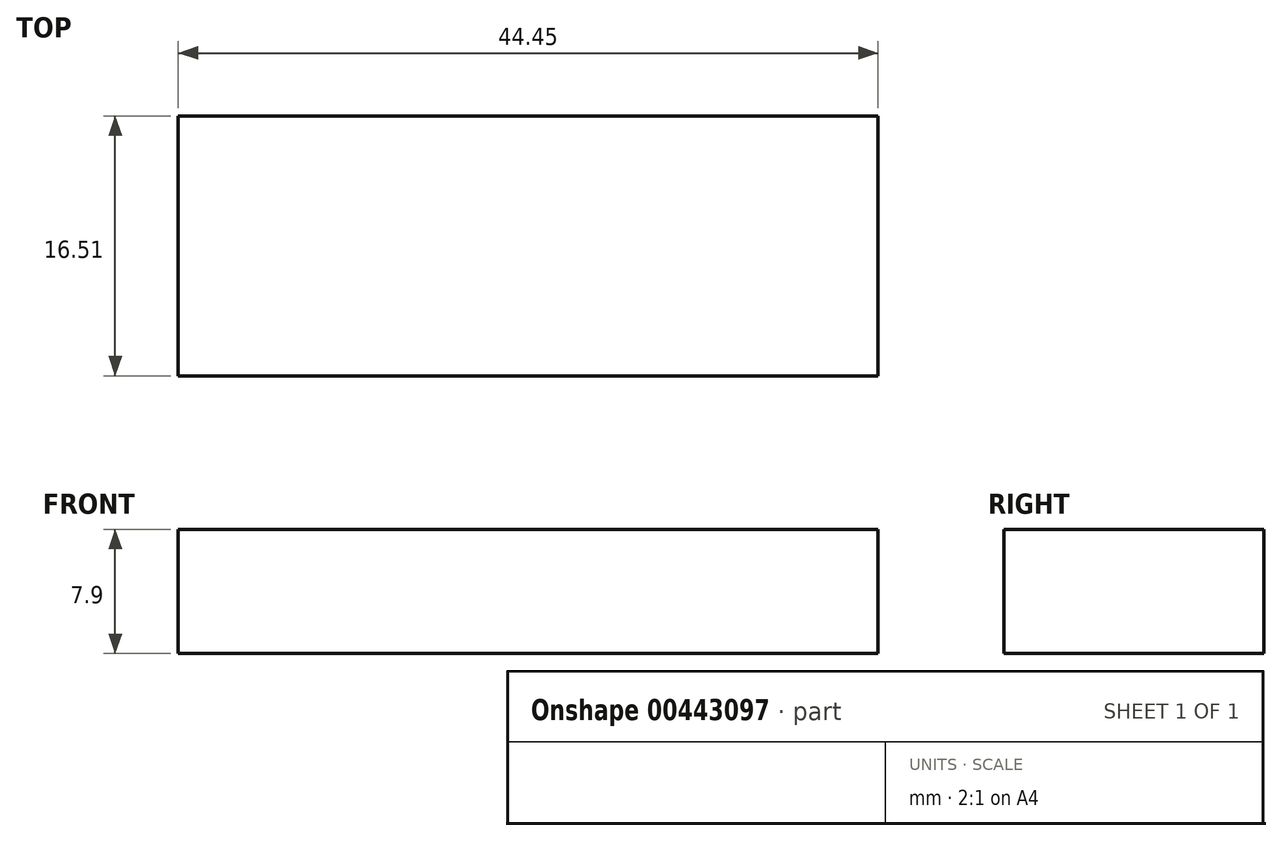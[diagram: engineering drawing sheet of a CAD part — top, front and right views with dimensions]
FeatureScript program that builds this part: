
annotation { "Feature Type Name" : "Feature", "Feature Type Description" : "" }
export const myFeature = defineFeature(function(context is Context, id is Id, definition is map)
    precondition{}
    {
        {
            var Q0;
            Q0=qCreatedBy(makeId("Top.planeOp"),FACE);
            var sketch = newSketch(context, id + "F0", { "sketchPlane" : qUnion([Q0])});
            skLineSegment(sketch, "E0.bottom", {"start": v(0, 0) * mm, "end": v(-50.8, 0) * mm});
            skLineSegment(sketch, "E0.top", {"start": v(0, 25.4) * mm, "end": v(-50.8, 25.4) * mm});
            skLineSegment(sketch, "E0.left", {"start": v(0, 0) * mm, "end": v(0, 25.4) * mm});
            skLineSegment(sketch, "E0.right", {"start": v(-50.8, 0) * mm, "end": v(-50.8, 25.4) * mm});
            skLineSegment(sketch, "E1.bottom", {"start": v(-44.45, 16.51) * mm, "end": v(0, 16.51) * mm});
            skLineSegment(sketch, "E1.top", {"start": v(-44.45, 0) * mm, "end": v(0, 0) * mm});
            skLineSegment(sketch, "E1.left", {"start": v(-44.45, 16.51) * mm, "end": v(-44.45, 0) * mm});
            skLineSegment(sketch, "E1.right", {"start": v(0, 16.51) * mm, "end": v(0, 0) * mm});
            skSolve(sketch);
        }
        {
            var Q0;
            Q0=makeQuery(id+"F0.imprint","IMPRINT",FACE,{"disambiguationData":[TD([[makeQuery(id+"F0.imprint","IMPRINT",EDGE,{"derivedFrom":sQuery(id+"F0.wireOp",EDGE,"E0.bottom")}),-1.0]])]});
            extrude(context, id + "F1", {"entities" : qUnion([Q0]), "depth" : 7.9 * mm});
        }
        {
            var Q0;
            Q0=makeQuery(id+"F1.opExtrude","CAP_FACE",FACE,{"disambiguationData":[OSD([sQuery(id+"F0.wireOp",EDGE,"E0.bottom"),sQuery(id+"F0.wireOp",EDGE,"E0.top"),sQuery(id+"F0.wireOp",EDGE,"E0.left"),sQuery(id+"F0.wireOp",EDGE,"E0.right"),sQuery(id+"F0.wireOp",EDGE,"E1.bottom"),sQuery(id+"F0.wireOp",EDGE,"E1.left")])],"isStart":true});
            var sketch = newSketch(context, id + "F2", { "sketchPlane" : qUnion([Q0])});
            skCircle(sketch, "E2", {"center": v(-8, -20.96) * mm, "radius": 1.5 * mm});
            skCircle(sketch, "E3", {"center": v(-13.25, -20.96) * mm, "radius": 1.5 * mm});
            skPoint(sketch, "E4", {"position": v(0, -20.96) * mm});
            skLineSegment(sketch, "E5", {"start": v(0, -20.96) * mm, "end": v(-17.36, -20.96) * mm});
            skSolve(sketch);
        }
        {
            var Q0;
            Q0 = qSketchRegion(id + "F2", true);
            extrude(context, id + "F3", {"entities" : qUnion([Q0]), "operationType" : NewBodyOperationType.REMOVE, "oppositeDirection" : true, "depth" : 25.4 * mm});
        }
    });
